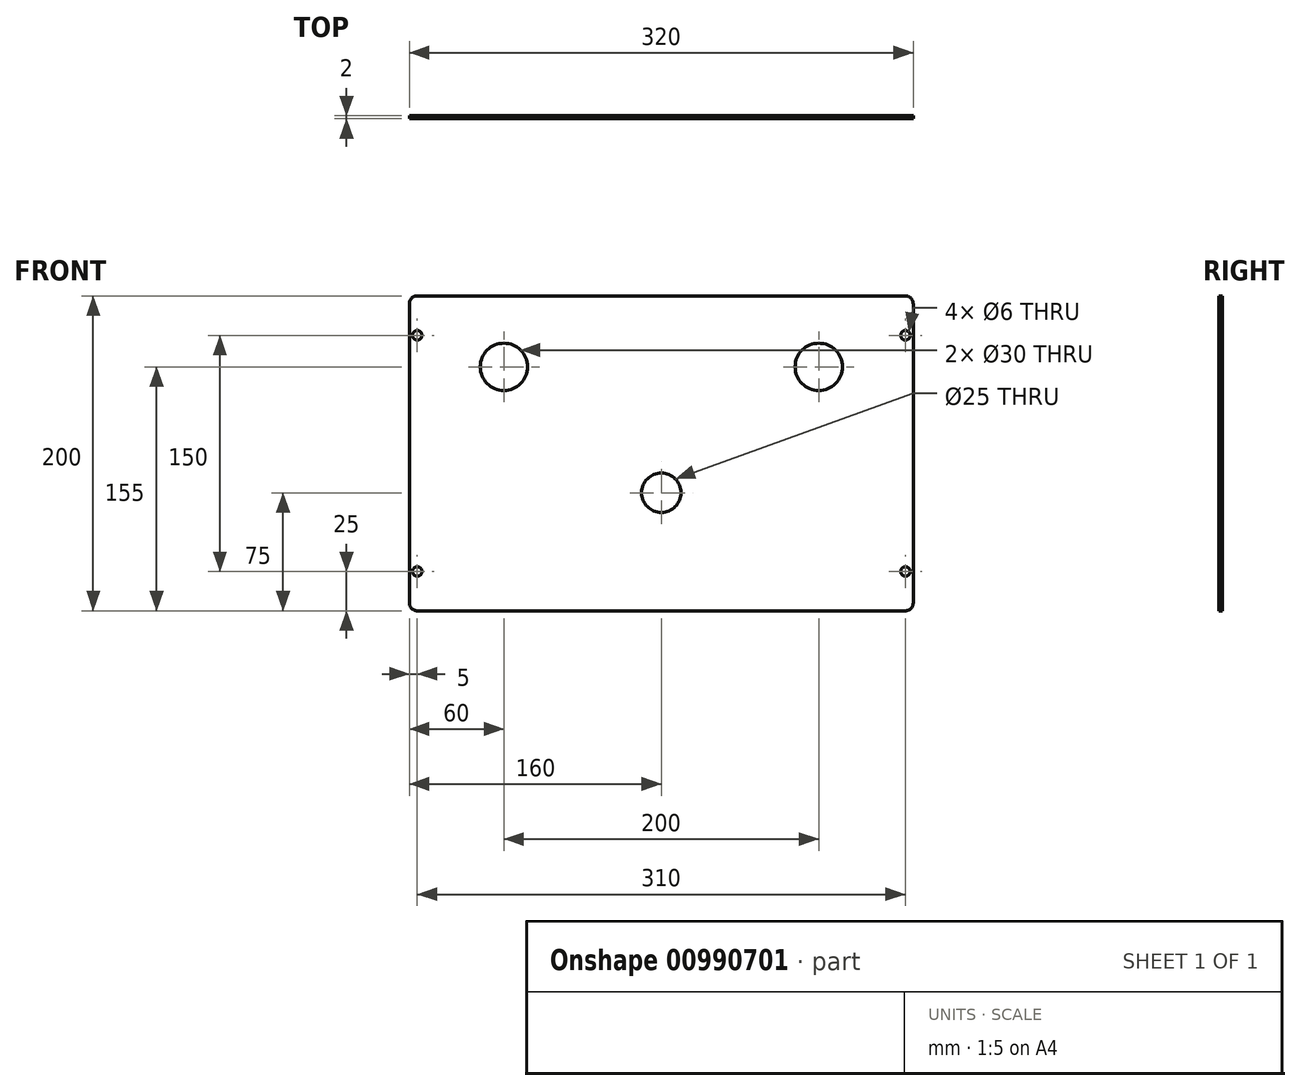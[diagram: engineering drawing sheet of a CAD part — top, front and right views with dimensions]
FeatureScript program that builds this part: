
annotation { "Feature Type Name" : "Feature", "Feature Type Description" : "" }
export const myFeature = defineFeature(function(context is Context, id is Id, definition is map)
    precondition{}
    {
        {
            var Q0;
            Q0=qCreatedBy(makeId("Front.planeOp"),FACE);
            var sketch = newSketch(context, id + "F0", { "sketchPlane" : qUnion([Q0])});
            skLineSegment(sketch, "E0.bottom", {"start": v(-155, 200) * mm, "end": v(155, 200) * mm});
            skLineSegment(sketch, "E0.top", {"start": v(-155, 0) * mm, "end": v(155, 0) * mm});
            skLineSegment(sketch, "E0.left", {"start": v(-160, 195) * mm, "end": v(-160, 5) * mm});
            skLineSegment(sketch, "E0.right", {"start": v(160, 195) * mm, "end": v(160, 5) * mm});
            skCircle(sketch, "E1", {"center": v(-155, 25) * mm, "radius": 3 * mm});
            skCircle(sketch, "E2", {"center": v(-155, 175) * mm, "radius": 3 * mm});
            skCircle(sketch, "E3", {"center": v(155, 175) * mm, "radius": 3 * mm});
            skCircle(sketch, "E4", {"center": v(155, 25) * mm, "radius": 3 * mm});
            skCircle(sketch, "E5", {"center": v(0, 75) * mm, "radius": 12.5 * mm});
            skCircle(sketch, "E6", {"center": v(-100, 155) * mm, "radius": 15 * mm});
            skCircle(sketch, "E7", {"center": v(100, 155) * mm, "radius": 15 * mm});
            skPoint(sketch, "E8.visualSharp", {"position": v(-160, 200) * mm});
            skArc(sketch, "E8.filletArc", {"start": v(-155, 200) * mm, "mid": v(-158.54, 198.54) * mm, "end": v(-160, 195) * mm});
            skPoint(sketch, "E9.visualSharp", {"position": v(-160, 0) * mm});
            skArc(sketch, "E9.filletArc", {"start": v(-160, 5) * mm, "mid": v(-158.54, 1.46) * mm, "end": v(-155, 0) * mm});
            skPoint(sketch, "E10.visualSharp", {"position": v(160, 0) * mm});
            skArc(sketch, "E10.filletArc", {"start": v(155, 0) * mm, "mid": v(158.54, 1.46) * mm, "end": v(160, 5) * mm});
            skPoint(sketch, "E11.visualSharp", {"position": v(160, 200) * mm});
            skArc(sketch, "E11.filletArc", {"start": v(160, 195) * mm, "mid": v(158.54, 198.54) * mm, "end": v(155, 200) * mm});
            skSolve(sketch);
        }
        {
            var Q0;
            Q0 = qSketchRegion(id + "F0", true);
            extrude(context, id + "F1", {"entities" : qUnion([Q0]), "depth" : 2 * mm, "offsetDistance" : 25 * mm});
        }
    });
